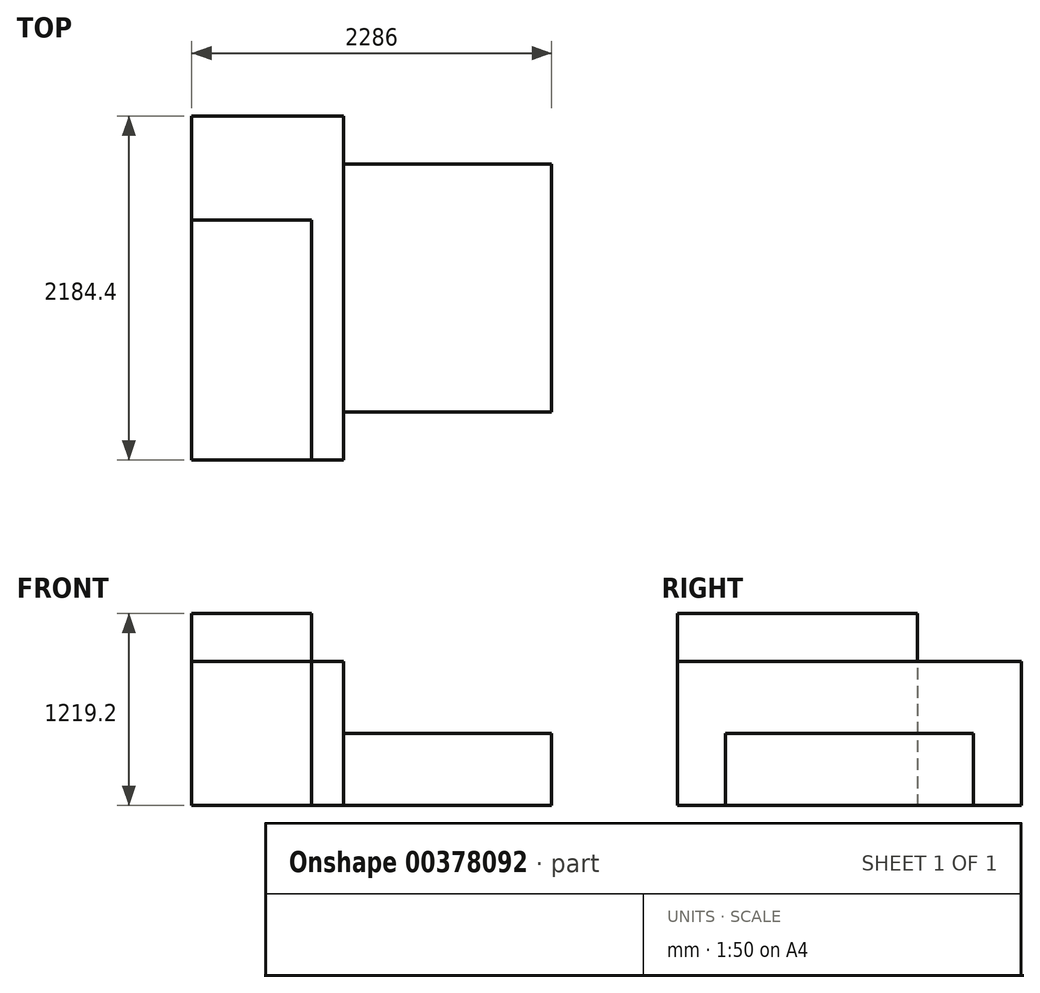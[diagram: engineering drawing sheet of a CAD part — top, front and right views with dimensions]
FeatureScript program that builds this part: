
annotation { "Feature Type Name" : "Feature", "Feature Type Description" : "" }
export const myFeature = defineFeature(function(context is Context, id is Id, definition is map)
    precondition{}
    {
        {
            var Q0;
            Q0=qCreatedBy(makeId("Top.planeOp"),FACE);
            var sketch = newSketch(context, id + "F0", { "sketchPlane" : qUnion([Q0])});
            skLineSegment(sketch, "E0.bottom", {"start": v(0, 0) * mm, "end": v(965.2, 0) * mm});
            skLineSegment(sketch, "E0.top", {"start": v(0, 2184.4) * mm, "end": v(965.2, 2184.4) * mm});
            skLineSegment(sketch, "E0.left", {"start": v(0, 0) * mm, "end": v(0, 2184.4) * mm});
            skLineSegment(sketch, "E0.right", {"start": v(965.2, 0) * mm, "end": v(965.2, 2184.4) * mm});
            skLineSegment(sketch, "E1", {"start": v(0, 1092.2) * mm, "end": v(2301.1, 1092.2) * mm, "construction": true});
            skLineSegment(sketch, "E2", {"start": v(965.2, 1879.6) * mm, "end": v(2286, 1879.6) * mm});
            skLineSegment(sketch, "E3", {"start": v(965.2, 304.8) * mm, "end": v(2286, 304.8) * mm});
            skLineSegment(sketch, "E4", {"start": v(2286, 304.8) * mm, "end": v(2286, 1879.6) * mm});
            skSolve(sketch);
        }
        {
            var Q0;
            Q0=makeQuery(id+"F0.imprint","IMPRINT",FACE,{"disambiguationData":[TD([[makeQuery(id+"F0.imprint","IMPRINT",EDGE,{"derivedFrom":sQuery(id+"F0.wireOp",EDGE,"E0.bottom")}),1.0]])]});
            extrude(context, id + "F1", {"entities" : qUnion([Q0]), "depth" : 914.4 * mm});
        }
        {
            var Q0;
            Q0=makeQuery(id+"F0.imprint","IMPRINT",FACE,{"disambiguationData":[TD([[makeQuery(id+"F0.imprint","IMPRINT",EDGE,{"derivedFrom":sQuery(id+"F0.wireOp",EDGE,"E0.right")}),-1.0]])]});
            extrude(context, id + "F2", {"entities" : qUnion([Q0]), "operationType" : NewBodyOperationType.ADD, "depth" : 457.2 * mm});
        }
        {
            var Q0;
            Q0=qCreatedBy(makeId("Top.planeOp"),FACE);
            var sketch = newSketch(context, id + "F3", { "sketchPlane" : qUnion([Q0])});
            skLineSegment(sketch, "E5.bottom", {"start": v(0, 0) * mm, "end": v(965.2, 0) * mm});
            skLineSegment(sketch, "E5.top", {"start": v(0, 1574.8) * mm, "end": v(965.2, 1574.8) * mm});
            skLineSegment(sketch, "E5.left", {"start": v(0, 0) * mm, "end": v(0, 1574.8) * mm});
            skLineSegment(sketch, "E5.right", {"start": v(965.2, 0) * mm, "end": v(965.2, 1574.8) * mm});
            skLineSegment(sketch, "E6.left", {"start": v(965.2, 1574.8) * mm, "end": v(965.2, 0) * mm});
            skLineSegment(sketch, "E7", {"start": v(965.2, 1270) * mm, "end": v(2286, 1270) * mm});
            skLineSegment(sketch, "E8", {"start": v(2286, 1270) * mm, "end": v(2286, 304.8) * mm});
            skLineSegment(sketch, "E9", {"start": v(2286, 304.8) * mm, "end": v(965.2, 304.8) * mm});
            skSolve(sketch);
        }
        {
            var Q0;
            Q0=makeQuery(id+"F3.imprint","IMPRINT",FACE,{"disambiguationData":[TD([[makeQuery(id+"F3.imprint","IMPRINT",EDGE,{"derivedFrom":sQuery(id+"F3.wireOp",EDGE,"E5.bottom")}),1.0]])]});
            extrude(context, id + "F4", {"entities" : qUnion([Q0]), "depth" : 914.4 * mm});
        }
        {
            var Q0;
            {var subQ0=sQuery(id+"F3.wireOp",EDGE,"E7");Q0=makeQuery(id+"F3.imprint","IMPRINT",FACE,{"disambiguationData":[TD([[makeQuery(id+"F3.imprint","IMPRINT",EDGE,{"derivedFrom":subQ0}),-1.0]])]});}
            extrude(context, id + "F5", {"entities" : qUnion([Q0]), "operationType" : NewBodyOperationType.ADD, "depth" : 457.2 * mm});
        }
        {
            var Q0;
            Q0=qCreatedBy(makeId("Top.planeOp"),FACE);
            var sketch = newSketch(context, id + "F6", { "sketchPlane" : qUnion([Q0])});
            skLineSegment(sketch, "E10.bottom", {"start": v(0, 0) * mm, "end": v(762, 0) * mm});
            skLineSegment(sketch, "E10.top", {"start": v(0, 1524) * mm, "end": v(762, 1524) * mm});
            skLineSegment(sketch, "E10.left", {"start": v(0, 0) * mm, "end": v(0, 1524) * mm});
            skLineSegment(sketch, "E10.right", {"start": v(762, 0) * mm, "end": v(762, 1524) * mm});
            skSolve(sketch);
        }
        {
            var Q0;
            Q0 = qSketchRegion(id + "F6", true);
            extrude(context, id + "F7", {"entities" : qUnion([Q0]), "depth" : 1219.2 * mm});
        }
    });
